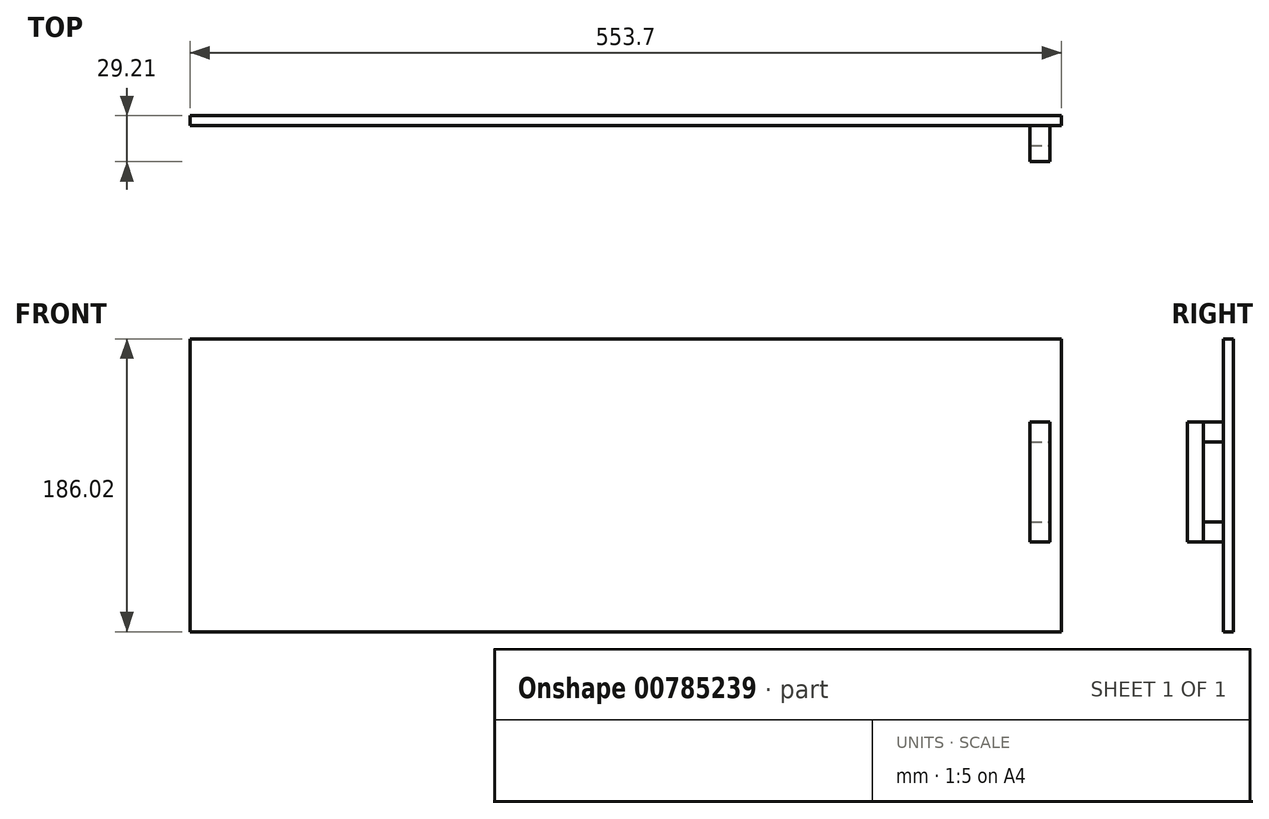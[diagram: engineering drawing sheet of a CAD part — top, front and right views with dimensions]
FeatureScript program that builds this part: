
annotation { "Feature Type Name" : "Feature", "Feature Type Description" : "" }
export const myFeature = defineFeature(function(context is Context, id is Id, definition is map)
    precondition{}
    {
        {
            var Q0;
            Q0=qCreatedBy(makeId("Front.planeOp"),FACE);
            var sketch = newSketch(context, id + "F0", { "sketchPlane" : qUnion([Q0])});
            skLineSegment(sketch, "E0.bottom", {"start": v(276.85, 93.01) * mm, "end": v(-276.85, 93.01) * mm});
            skLineSegment(sketch, "E0.top", {"start": v(276.85, -93.01) * mm, "end": v(-276.85, -93.01) * mm});
            skLineSegment(sketch, "E0.left", {"start": v(276.85, 93.01) * mm, "end": v(276.85, -93.01) * mm});
            skLineSegment(sketch, "E0.right", {"start": v(-276.85, 93.01) * mm, "end": v(-276.85, -93.01) * mm});
            skPoint(sketch, "E0.middle", {"position": v(0, 0) * mm});
            skSolve(sketch);
        }
        {
            var Q0;
            Q0=makeQuery(id+"F0.imprint","IMPRINT",FACE,{"disambiguationData":[TD([[makeQuery(id+"F0.imprint","IMPRINT",EDGE,{"derivedFrom":sQuery(id+"F0.wireOp",EDGE,"E0.bottom")}),1.0]])]});
            extrude(context, id + "F1", {"entities" : qUnion([Q0]), "depth" : 6.35 * mm, "offsetDistance" : 25.4 * mm});
        }
        {
            var Q0;
            Q0=makeQuery(id+"F1.opExtrude","CAP_FACE",FACE,{"disambiguationData":[OSD([sQuery(id+"F0.wireOp",EDGE,"E0.bottom"),sQuery(id+"F0.wireOp",EDGE,"E0.top"),sQuery(id+"F0.wireOp",EDGE,"E0.left"),sQuery(id+"F0.wireOp",EDGE,"E0.right")])],"isStart":false});
            var sketch = newSketch(context, id + "F2", { "sketchPlane" : qUnion([Q0])});
            skLineSegment(sketch, "E1.bottom", {"start": v(256.7, -23.16) * mm, "end": v(269.4, -23.16) * mm});
            skLineSegment(sketch, "E1.top", {"start": v(256.7, -35.86) * mm, "end": v(269.4, -35.86) * mm});
            skLineSegment(sketch, "E1.left", {"start": v(256.7, -23.16) * mm, "end": v(256.7, -35.86) * mm});
            skLineSegment(sketch, "E1.right", {"start": v(269.4, -23.16) * mm, "end": v(269.4, -35.86) * mm});
            skLineSegment(sketch, "E2.bottom", {"start": v(256.7, 27.64) * mm, "end": v(269.4, 27.64) * mm});
            skLineSegment(sketch, "E2.top", {"start": v(256.7, 40.34) * mm, "end": v(269.4, 40.34) * mm});
            skLineSegment(sketch, "E2.left", {"start": v(256.7, 27.64) * mm, "end": v(256.7, 40.34) * mm});
            skLineSegment(sketch, "E2.right", {"start": v(269.4, 27.64) * mm, "end": v(269.4, 40.34) * mm});
            skSolve(sketch);
        }
        {
            var Q0;
            Q0 = qSketchRegion(id + "F2", true);
            extrude(context, id + "F3", {"entities" : qUnion([Q0]), "operationType" : NewBodyOperationType.ADD, "depth" : 12.7 * mm, "offsetDistance" : 25.4 * mm});
        }
        {
            var Q0;
            Q0=makeQuery(id+"F3.opExtrude","CAP_FACE",FACE,{"disambiguationData":[OSD([sQuery(id+"F2.wireOp",EDGE,"E2.bottom"),sQuery(id+"F2.wireOp",EDGE,"E2.top"),sQuery(id+"F2.wireOp",EDGE,"E2.left"),sQuery(id+"F2.wireOp",EDGE,"E2.right")])],"isStart":false});
            var sketch = newSketch(context, id + "F4", { "sketchPlane" : qUnion([Q0])});
            skLineSegment(sketch, "E3.bottom", {"start": v(256.7, 40.34) * mm, "end": v(269.38, 40.34) * mm});
            skLineSegment(sketch, "E3.top", {"start": v(256.7, -35.86) * mm, "end": v(269.38, -35.86) * mm});
            skLineSegment(sketch, "E3.left", {"start": v(256.7, 40.34) * mm, "end": v(256.7, -35.86) * mm});
            skLineSegment(sketch, "E3.right", {"start": v(269.38, 40.34) * mm, "end": v(269.38, -35.86) * mm});
            skSolve(sketch);
        }
        {
            var Q0;
            Q0 = qSketchRegion(id + "F4", true);
            extrude(context, id + "F5", {"entities" : qUnion([Q0]), "operationType" : NewBodyOperationType.ADD, "depth" : 10.16 * mm, "offsetDistance" : 25.4 * mm});
        }
    });
